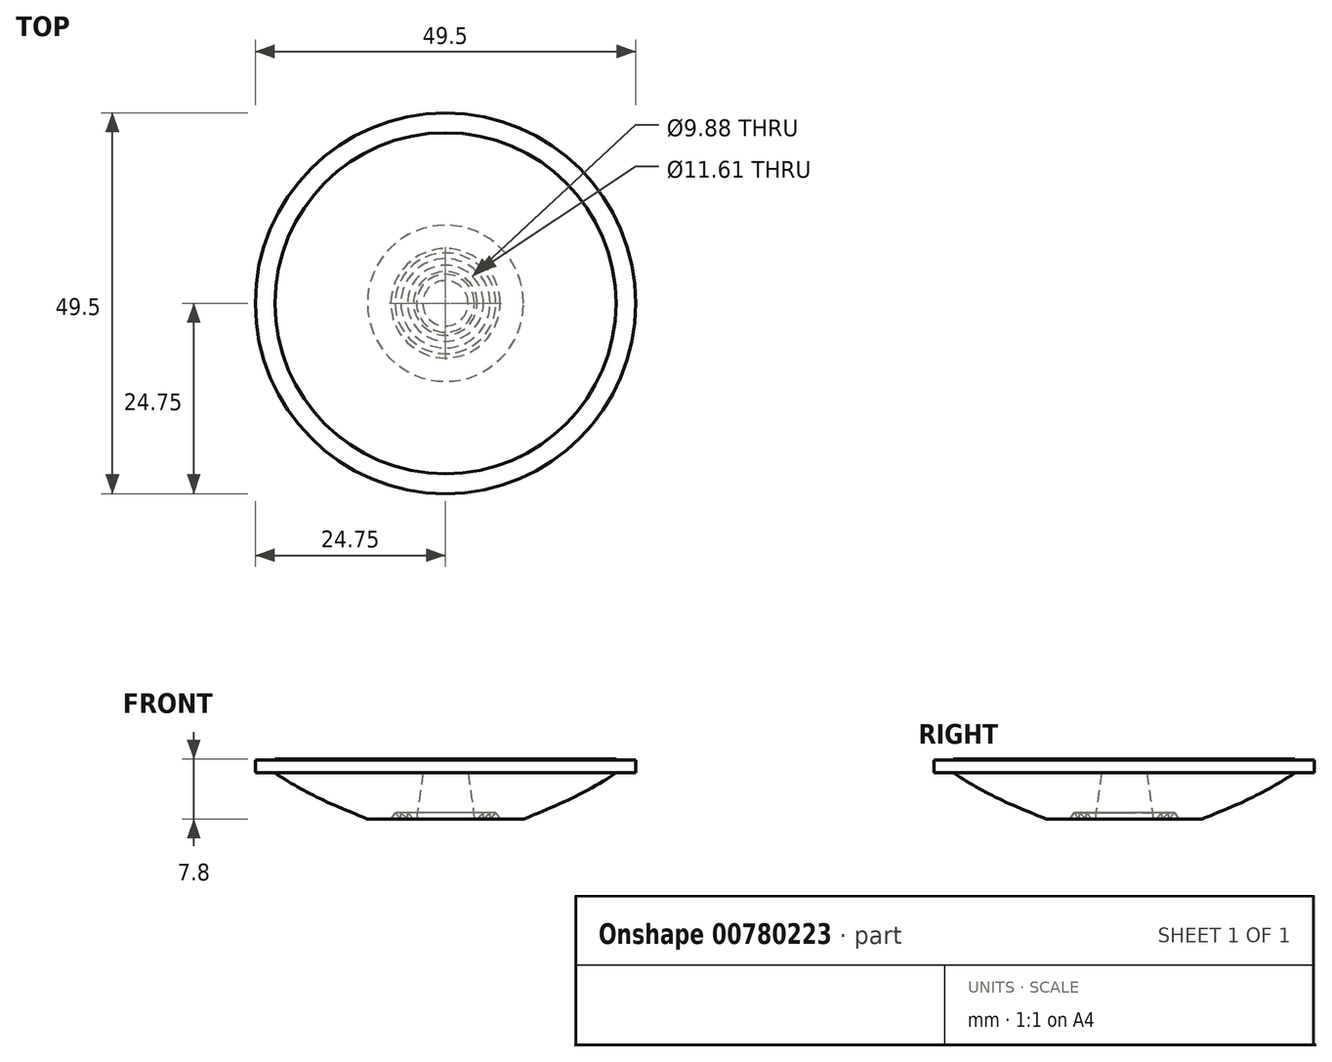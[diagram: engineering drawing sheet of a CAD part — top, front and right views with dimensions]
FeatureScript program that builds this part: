
annotation { "Feature Type Name" : "Feature", "Feature Type Description" : "" }
export const myFeature = defineFeature(function(context is Context, id is Id, definition is map)
    precondition{}
    {
        {
            var Q0;
            Q0=qCreatedBy(makeId("Front.planeOp"),FACE);
            var sketch = newSketch(context, id + "F0", { "sketchPlane" : qUnion([Q0])});
            skLineSegment(sketch, "E0", {"start": v(0, 0) * mm, "end": v(22.18, 0) * mm});
            skLineSegment(sketch, "E1", {"start": v(24.75, -0.1) * mm, "end": v(24.75, -1.8) * mm});
            skLineSegment(sketch, "E2", {"start": v(0, 0) * mm, "end": v(0, -1.8) * mm});
            skLineSegment(sketch, "E3", {"start": v(0, -1.8) * mm, "end": v(2.95, -1.8) * mm});
            skLineSegment(sketch, "E4", {"start": v(22.2, -1.8) * mm, "end": v(24.75, -1.8) * mm});
            skLineSegment(sketch, "E5", {"start": v(3.77, -7.8) * mm, "end": v(4.14, -7.8) * mm});
            skFitSpline(sketch, "E6", {"points": [v(10.16, -7.8) * mm, v(16.9, -4.87) * mm, v(22.2, -1.8) * mm], "startDerivative": vector(15.68, 6.32) * mm, "endDerivative": vector(7.93, 5.64) * mm});
            skLineSegment(sketch, "E7", {"start": v(3.77, -7.8) * mm, "end": v(2.95, -1.8) * mm});
            skLineSegment(sketch, "E8", {"start": v(4.14, -7.8) * mm, "end": v(4.94, -7) * mm});
            skLineSegment(sketch, "E9", {"start": v(4.94, -7) * mm, "end": v(4.94, -7.8) * mm});
            skLineSegment(sketch, "E10", {"start": v(4.94, -7.8) * mm, "end": v(5.8, -7) * mm});
            skLineSegment(sketch, "E11", {"start": v(5.8, -7) * mm, "end": v(5.8, -7.8) * mm});
            skLineSegment(sketch, "E12", {"start": v(5.8, -7.8) * mm, "end": v(6.55, -7) * mm});
            skLineSegment(sketch, "E13", {"start": v(6.55, -7) * mm, "end": v(7.1, -7.8) * mm});
            skLineSegment(sketch, "E14.trimOffspring", {"start": v(7.1, -7.8) * mm, "end": v(10.16, -7.8) * mm});
            skLineSegment(sketch, "E15.top", {"start": v(24.75, -0.1) * mm, "end": v(22.18, -0.1) * mm});
            skLineSegment(sketch, "E15.right", {"start": v(22.18, 0) * mm, "end": v(22.18, -0.1) * mm});
            skSolve(sketch);
        }
        {
            var Q0;
            Q0=makeQuery(id+"F0.imprint","IMPRINT",FACE,{"disambiguationData":[TD([[makeQuery(id+"F0.imprint","IMPRINT",EDGE,{"derivedFrom":sQuery(id+"F0.wireOp",EDGE,"E0")}),-1.0]])]});
            var Q1;
            Q1=sQuery(id+"F0.wireOp",EDGE,"E2");
            revolve(context, id + "F1", {"surfaceOperationType" : NewSurfaceOperationType.NEW, "entities" : qUnion([Q0]), "axis" : qUnion([Q1]), "revolveType" : RevolveType.FULL});
        }
    });
